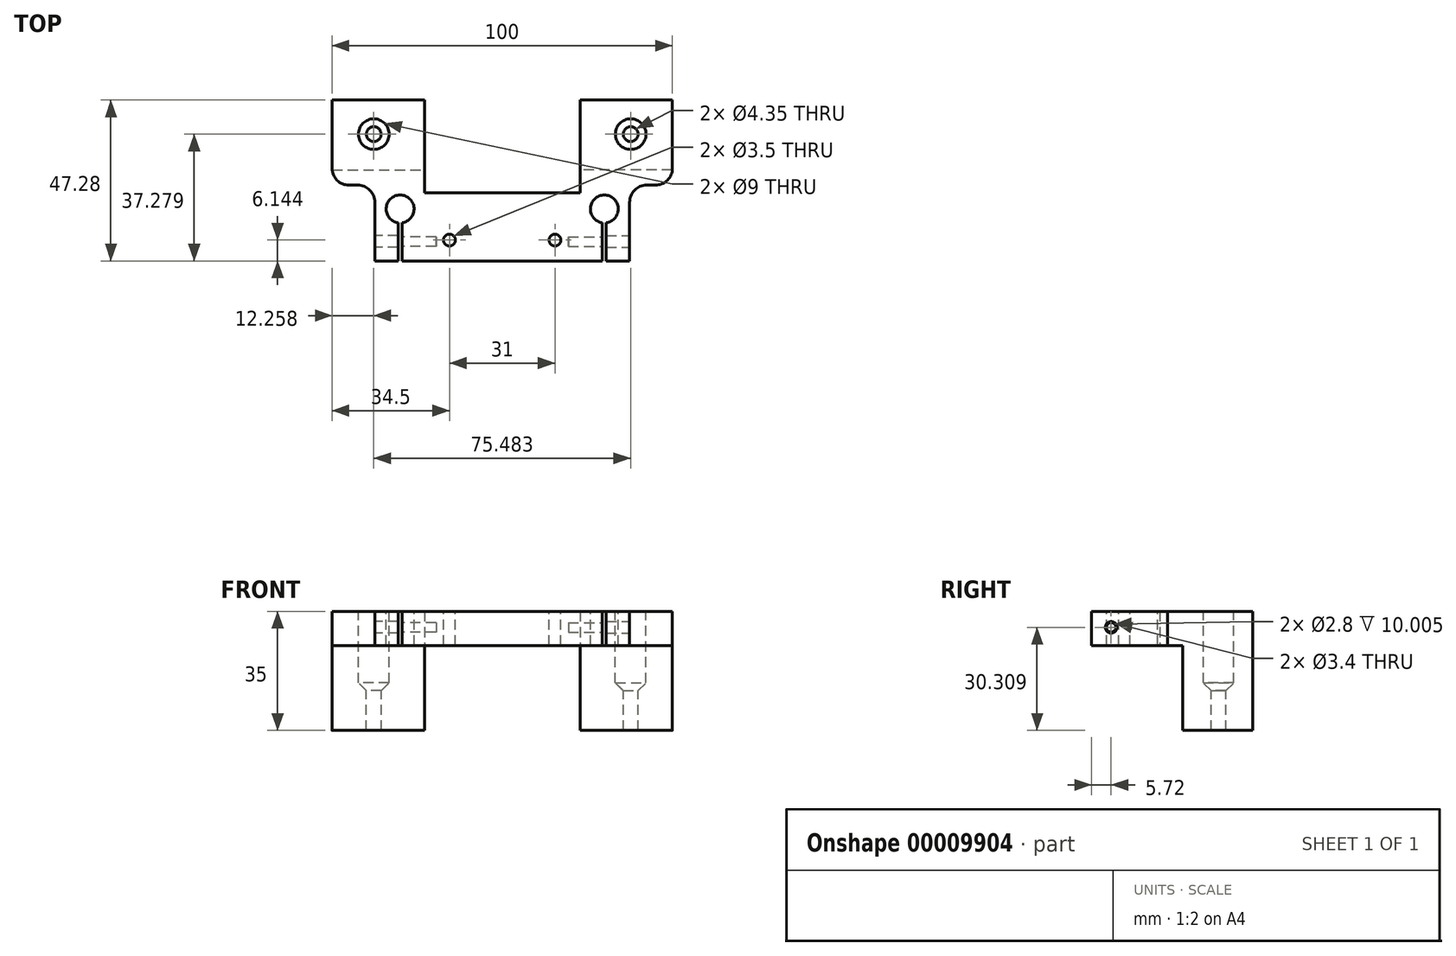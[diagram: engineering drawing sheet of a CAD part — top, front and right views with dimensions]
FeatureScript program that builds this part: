
annotation { "Feature Type Name" : "Feature", "Feature Type Description" : "" }
export const myFeature = defineFeature(function(context is Context, id is Id, definition is map)
    precondition{}
    {
        {
            var Q0;
            Q0=qCreatedBy(makeId("Top.planeOp"),FACE);
            var sketch = newSketch(context, id + "F0", { "sketchPlane" : qUnion([Q0])});
            skLineSegment(sketch, "E0", {"start": v(0, -13.82) * mm, "end": v(-37.44, -13.82) * mm});
            skLineSegment(sketch, "E1", {"start": v(-37.44, -13.82) * mm, "end": v(-37.44, 8.46) * mm});
            skLineSegment(sketch, "E2", {"start": v(-37.44, 8.46) * mm, "end": v(-50, 8.46) * mm});
            skLineSegment(sketch, "E3", {"start": v(-50, 8.46) * mm, "end": v(-50, 33.46) * mm});
            skLineSegment(sketch, "E4", {"start": v(-50, 33.46) * mm, "end": v(-22.87, 33.46) * mm});
            skLineSegment(sketch, "E5", {"start": v(-22.87, 33.46) * mm, "end": v(-22.87, 6.18) * mm});
            skLineSegment(sketch, "E6", {"start": v(-22.87, 6.18) * mm, "end": v(0, 6.18) * mm});
            skLineSegment(sketch, "E7", {"start": v(0, 6.18) * mm, "end": v(0, -13.82) * mm});
            skSolve(sketch);
        }
        {
            var Q0;
            Q0=qSketchRegion(id+"F0",true);
            extrude(context, id + "F1", {"entities" : qUnion([Q0]), "depth" : 10 * mm});
        }
        {
            var Q0;
            Q0=makeQuery(id+"F1.opExtrude","CAP_FACE",FACE,{"disambiguationData":[OSD([sQuery(id+"F0.wireOp",EDGE,"E0"),sQuery(id+"F0.wireOp",EDGE,"E1"),sQuery(id+"F0.wireOp",EDGE,"E2"),sQuery(id+"F0.wireOp",EDGE,"E3"),sQuery(id+"F0.wireOp",EDGE,"E4"),sQuery(id+"F0.wireOp",EDGE,"E5"),sQuery(id+"F0.wireOp",EDGE,"E6"),sQuery(id+"F0.wireOp",EDGE,"E7")])],"isStart":true});
            var sketch = newSketch(context, id + "F2", { "sketchPlane" : qUnion([Q0])});
            skLineSegment(sketch, "E8.bottom", {"start": v(-50, -33.46) * mm, "end": v(-22.87, -33.46) * mm});
            skLineSegment(sketch, "E8.top", {"start": v(-50, -12.92) * mm, "end": v(-22.87, -12.92) * mm});
            skLineSegment(sketch, "E8.left", {"start": v(-50, -33.46) * mm, "end": v(-50, -12.92) * mm});
            skLineSegment(sketch, "E8.right", {"start": v(-22.87, -33.46) * mm, "end": v(-22.87, -12.92) * mm});
            skSolve(sketch);
        }
        {
            var Q0;
            Q0 = qSketchRegion(id + "F2", true);
            extrude(context, id + "F3", {"entities" : qUnion([Q0]), "operationType" : NewBodyOperationType.ADD, "depth" : 25 * mm});
        }
        {
            var Q0;
            {var subQ0=makeQuery(id+"F1.opExtrude","CAP_FACE",FACE,{"disambiguationData":[OSD([sQuery(id+"F0.wireOp",EDGE,"E0"),sQuery(id+"F0.wireOp",EDGE,"fd64a43a-5635-4f94-a977-4dd36923accb"),sQuery(id+"F0.wireOp",EDGE,"1334f7d4-4c90-4769-8fa3-fe5f576fb005"),sQuery(id+"F0.wireOp",EDGE,"E1"),sQuery(id+"F0.wireOp",EDGE,"E2"),sQuery(id+"F0.wireOp",EDGE,"E3"),sQuery(id+"F0.wireOp",EDGE,"E4"),sQuery(id+"F0.wireOp",EDGE,"E5"),sQuery(id+"F0.wireOp",EDGE,"E6"),sQuery(id+"F0.wireOp",EDGE,"E7")])],"isStart":false});Q0=makeQuery(id+"F15.boolean.opBoolean","MERGE",FACE,{"derivedFrom":[subQ0,makeQuery(id+"F15.opPattern","COPY",FACE,{"derivedFrom":subQ0,"instanceName":"1"})]});}
            var sketch = newSketch(context, id + "F4", { "sketchPlane" : qUnion([Q0])});
            skCircle(sketch, "E9", {"center": v(-30, 1.46) * mm, "radius": 4.1 * mm});
            skCircle(sketch, "E10", {"center": v(-37.74, 23.46) * mm, "radius": 2.17 * mm});
            skLineSegment(sketch, "E11", {"start": v(-30, 1.46) * mm, "end": v(-30, -13.82) * mm, "construction": true});
            skLineSegment(sketch, "E12.bottom", {"start": v(-30.55, -1.63) * mm, "end": v(-29.45, -1.63) * mm});
            skLineSegment(sketch, "E12.top", {"start": v(-30.55, -14.74) * mm, "end": v(-29.45, -14.74) * mm});
            skLineSegment(sketch, "E12.left", {"start": v(-30.55, -1.63) * mm, "end": v(-30.55, -14.74) * mm});
            skLineSegment(sketch, "E12.right", {"start": v(-29.45, -1.63) * mm, "end": v(-29.45, -14.74) * mm});
            skPoint(sketch, "E13", {"position": v(-30, -1.63) * mm});
            skCircle(sketch, "E14", {"center": v(-37.74, 23.46) * mm, "radius": 4.5 * mm});
            skSolve(sketch);
        }
        {
            var Q0;
            {var subQ3=sQuery(id+"F4.wireOp",EDGE,"E12.bottom");Q0=makeQuery(id+"F4.imprint","IMPRINT",FACE,{"disambiguationData":[TD([[makeQuery(id+"F4.imprint","IMPRINT",EDGE,{"derivedFrom":subQ3}),1.0]])]});}
            var Q1;
            {var subQ5=sQuery(id+"F4.wireOp",EDGE,"E12.top");Q1=makeQuery(id+"F4.imprint","IMPRINT",FACE,{"disambiguationData":[TD([[makeQuery(id+"F4.imprint","IMPRINT",EDGE,{"derivedFrom":subQ5}),1.0]])]});}
            var Q2;
            {var subQ3=sQuery(id+"F4.wireOp",EDGE,"E12.left");var subQ5=sQuery(id+"F4.wireOp",EDGE,"E9");var subQ7=makeQuery(id+"F4.imprint","INTERSECT",VERTEX,{"derivedFrom":[subQ5,subQ3]});Q2=makeQuery(id+"F4.imprint","IMPRINT",FACE,{"disambiguationData":[TD([[makeQuery(id+"F4.imprint","IMPRINT",EDGE,{"disambiguationData":[TD([[subQ7,-1.0]])],"derivedFrom":subQ5}),-1.0]])]});}
            var Q3;
            {var subQ3=sQuery(id+"F4.wireOp",EDGE,"E12.bottom");Q3=makeQuery(id+"F4.imprint","IMPRINT",FACE,{"disambiguationData":[TD([[makeQuery(id+"F4.imprint","IMPRINT",EDGE,{"derivedFrom":subQ3}),-1.0]])]});}
            var Q4;
            Q4=makeQuery(id+"F4.imprint","IMPRINT",FACE,{"disambiguationData":[TD([[makeQuery(id+"F4.imprint","IMPRINT",EDGE,{"derivedFrom":sQuery(id+"F4.wireOp",EDGE,"E10")}),1.0]])]});
            extrude(context, id + "F5", {"entities" : qUnion([Q0, Q1, Q2, Q3, Q4]), "operationType" : NewBodyOperationType.REMOVE, "endBound" : BoundingType.THROUGH_ALL, "oppositeDirection" : true, "depth" : 25 * mm});
        }
        {
            var Q0;
            Q0=makeQuery(id+"F1.opExtrude","SWEPT_EDGE",EDGE,{"disambiguationData":[OSD([sQuery(id+"F0.wireOp",EDGE,"E2"),sQuery(id+"F0.wireOp",EDGE,"E3")])]});
            fillet(context, id + "F6", {"entities" : qUnion([Q0]), "radius" : 5 * mm, "tangentPropagation" : true, "allowEdgeOverflow" : false});
        }
        {
            var Q0;
            Q0=makeQuery(id+"F1.opExtrude","SWEPT_EDGE",EDGE,{"disambiguationData":[OSD([sQuery(id+"F0.wireOp",EDGE,"E1"),sQuery(id+"F0.wireOp",EDGE,"E2")])]});
            fillet(context, id + "F7", {"entities" : qUnion([Q0]), "radius" : 5 * mm, "tangentPropagation" : true, "allowEdgeOverflow" : false});
        }
        {
            var Q0;
            Q0=makeQuery(id+"F1.opExtrude","SWEPT_FACE",FACE,{"disambiguationData":[OSD([sQuery(id+"F0.wireOp",EDGE,"E1")])]});
            var sketch = newSketch(context, id + "F8", { "sketchPlane" : qUnion([Q0])});
            skCircle(sketch, "E15", {"center": v(8.1, 5.3) * mm, "radius": 1.7 * mm});
            skCircle(sketch, "E16", {"center": v(8.1, 5.3) * mm, "radius": 1.4 * mm});
            skSolve(sketch);
        }
        {
            var Q0;
            Q0=makeQuery(id+"F8.imprint","IMPRINT",FACE,{"disambiguationData":[TD([[makeQuery(id+"F8.imprint","IMPRINT",EDGE,{"derivedFrom":sQuery(id+"F8.wireOp",EDGE,"E16")}),1.0]])]});
            extrude(context, id + "F9", {"entities" : qUnion([Q0]), "operationType" : NewBodyOperationType.REMOVE, "oppositeDirection" : true, "depth" : 18 * mm});
        }
        {
            var Q0;
            Q0=makeQuery(id+"F8.imprint","IMPRINT",FACE,{"disambiguationData":[TD([[makeQuery(id+"F8.imprint","IMPRINT",EDGE,{"derivedFrom":sQuery(id+"F8.wireOp",EDGE,"E16")}),1.0]])]});
            var Q1;
            Q1=makeQuery(id+"F8.imprint","IMPRINT",FACE,{"disambiguationData":[TD([[makeQuery(id+"F8.imprint","IMPRINT",EDGE,{"derivedFrom":sQuery(id+"F8.wireOp",EDGE,"E15")}),1.0]])]});
            extrude(context, id + "F10", {"entities" : qUnion([Q0, Q1]), "operationType" : NewBodyOperationType.REMOVE, "endBound" : BoundingType.UP_TO_NEXT, "oppositeDirection" : true, "depth" : 25 * mm});
        }
        {
            var Q0;
            Q0=makeQuery(id+"F1.opExtrude","CAP_FACE",FACE,{"disambiguationData":[OSD([sQuery(id+"F0.wireOp",EDGE,"E0"),sQuery(id+"F0.wireOp",EDGE,"E1"),sQuery(id+"F0.wireOp",EDGE,"E2"),sQuery(id+"F0.wireOp",EDGE,"E3"),sQuery(id+"F0.wireOp",EDGE,"E4"),sQuery(id+"F0.wireOp",EDGE,"E5"),sQuery(id+"F0.wireOp",EDGE,"E6"),sQuery(id+"F0.wireOp",EDGE,"E7")])],"isStart":false});
            var sketch = newSketch(context, id + "F11", { "sketchPlane" : qUnion([Q0])});
            skCircle(sketch, "E17", {"center": v(-15.5, -7.68) * mm, "radius": 1.75 * mm});
            skPoint(sketch, "E17.centerSnap0", {"position": v(0, -7.68) * mm});
            skSolve(sketch);
        }
        {
            var Q0;
            Q0=makeQuery(id+"F11.imprint","IMPRINT",FACE,{"disambiguationData":[TD([[makeQuery(id+"F11.imprint","IMPRINT",EDGE,{"derivedFrom":sQuery(id+"F11.wireOp",EDGE,"E17")}),1.0]])]});
            extrude(context, id + "F12", {"entities" : qUnion([Q0]), "operationType" : NewBodyOperationType.REMOVE, "oppositeDirection" : true, "depth" : 25 * mm});
        }
        {
            var Q0;
            Q0=makeQuery(id+"F4.imprint","IMPRINT",FACE,{"disambiguationData":[TD([[makeQuery(id+"F4.imprint","IMPRINT",EDGE,{"derivedFrom":sQuery(id+"F4.wireOp",EDGE,"E10")}),-1.0]])]});
            extrude(context, id + "F13", {"entities" : qUnion([Q0]), "operationType" : NewBodyOperationType.REMOVE, "oppositeDirection" : true, "depth" : 25 * mm});
        }
        {
            var Q0;
            Q0=makeQuery(id+"F13.boolean.opBoolean","COPY",EDGE,{"derivedFrom":makeQuery(id+"F13.opExtrude","CAP_EDGE",EDGE,{"disambiguationData":[OSD([sQuery(id+"F4.wireOp",EDGE,"E14")])],"isStart":false})});
            chamfer(context, id + "F14", {"entities" : qUnion([Q0]), "width" : 4 * mm, "tangentPropagation" : true});
        }
        {
            var Q0;
            Q0=makeQuery(id+"F1.opExtrude","SWEPT_BODY",BODY,{"disambiguationData":[OSD([sQuery(id+"F0.wireOp",EDGE,"E0"),sQuery(id+"F0.wireOp",EDGE,"fd64a43a-5635-4f94-a977-4dd36923accb"),sQuery(id+"F0.wireOp",EDGE,"1334f7d4-4c90-4769-8fa3-fe5f576fb005"),sQuery(id+"F0.wireOp",EDGE,"E1"),sQuery(id+"F0.wireOp",EDGE,"E2"),sQuery(id+"F0.wireOp",EDGE,"E3"),sQuery(id+"F0.wireOp",EDGE,"E4"),sQuery(id+"F0.wireOp",EDGE,"E5"),sQuery(id+"F0.wireOp",EDGE,"E6"),sQuery(id+"F0.wireOp",EDGE,"E7")])]});
            var Q1;
            Q1=qCreatedBy(makeId("Right.planeOp"),FACE);
            mirror(context, id + "F15", {"operationType" : NewBodyOperationType.ADD, "entities" : qUnion([Q0]), "mirrorPlane" : qUnion([Q1])});
        }
    });
